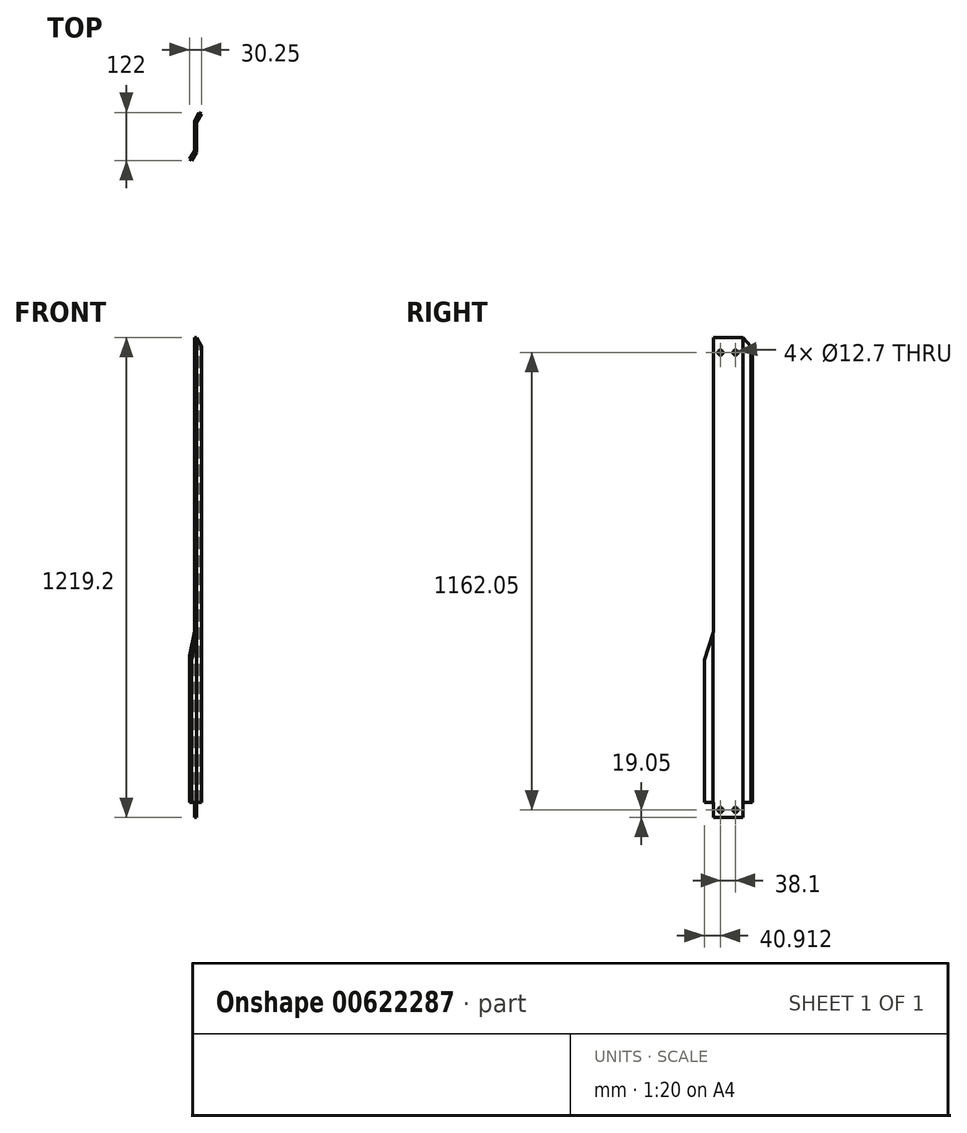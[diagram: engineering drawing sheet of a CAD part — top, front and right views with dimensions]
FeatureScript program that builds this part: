
annotation { "Feature Type Name" : "Feature", "Feature Type Description" : "" }
export const myFeature = defineFeature(function(context is Context, id is Id, definition is map)
    precondition{}
    {
        {
            var Q0;
            Q0=qCreatedBy(makeId("Top.planeOp"),FACE);
            var sketch = newSketch(context, id + "F0", { "sketchPlane" : qUnion([Q0])});
            skLineSegment(sketch, "E0.left", {"start": v(0, 0) * mm, "end": v(0, 76.2) * mm});
            skLineSegment(sketch, "E0.right", {"start": v(5.88, -1.67) * mm, "end": v(5.88, 74.53) * mm});
            skLineSegment(sketch, "E1", {"start": v(0, 76.2) * mm, "end": v(12.2, 98.47) * mm});
            skLineSegment(sketch, "E2", {"start": v(12.2, 98.47) * mm, "end": v(17.78, 95.42) * mm});
            skLineSegment(sketch, "E3", {"start": v(17.78, 95.42) * mm, "end": v(5.88, 74.53) * mm});
            skLineSegment(sketch, "E4", {"start": v(0, 0) * mm, "end": v(-12.47, -20.19) * mm});
            skLineSegment(sketch, "E5", {"start": v(-12.47, -20.19) * mm, "end": v(-7.06, -23.53) * mm});
            skLineSegment(sketch, "E6", {"start": v(-7.06, -23.53) * mm, "end": v(5.88, -1.67) * mm});
            skSolve(sketch);
        }
        {
            var Q0;
            Q0=makeQuery(id+"F0.imprint","IMPRINT",FACE,{"disambiguationData":[TD([[makeQuery(id+"F0.imprint","IMPRINT",EDGE,{"derivedFrom":sQuery(id+"F0.wireOp",EDGE,"E0.left")}),-1.0]])]});
            extrude(context, id + "F1", {"entities" : qUnion([Q0]), "oppositeDirection" : true, "depth" : 1219.2 * mm, "offsetDistance" : 25.4 * mm});
        }
        {
            var Q0;
            Q0=qCreatedBy(makeId("Right.planeOp"),FACE);
            var sketch = newSketch(context, id + "F2", { "sketchPlane" : qUnion([Q0])});
            skLineSegment(sketch, "E7.bottom", {"start": v(74.53, -1219.2) * mm, "end": v(98.47, -1219.2) * mm});
            skLineSegment(sketch, "E7.top", {"start": v(74.53, -1181.1) * mm, "end": v(98.47, -1181.1) * mm});
            skLineSegment(sketch, "E7.left", {"start": v(74.53, -1219.2) * mm, "end": v(74.53, -1181.1) * mm});
            skLineSegment(sketch, "E7.right", {"start": v(98.47, -1219.2) * mm, "end": v(98.47, -1181.1) * mm});
            skSolve(sketch);
        }
        {
            var Q0;
            Q0=makeQuery(id+"F2.imprint","IMPRINT",FACE,{"disambiguationData":[TD([[makeQuery(id+"F2.imprint","IMPRINT",EDGE,{"derivedFrom":sQuery(id+"F2.wireOp",EDGE,"E7.bottom")}),1.0]])]});
            extrude(context, id + "F3", {"entities" : qUnion([Q0]), "operationType" : NewBodyOperationType.REMOVE, "endBound" : BoundingType.THROUGH_ALL, "depth" : 25.4 * mm, "offsetDistance" : 25.4 * mm});
        }
        {
            var Q0;
            Q0=makeQuery(id+"F1.opExtrude","SWEPT_FACE",FACE,{"disambiguationData":[OSD([sQuery(id+"F0.wireOp",EDGE,"E0.right")])]});
            var sketch = newSketch(context, id + "F4", { "sketchPlane" : qUnion([Q0])});
            skPoint(sketch, "E8", {"position": v(17.38, -1200.15) * mm});
            skPoint(sketch, "E9", {"position": v(55.48, -1200.15) * mm});
            skPoint(sketch, "E10", {"position": v(98.49, -25.4) * mm});
            skPoint(sketch, "E11", {"position": v(-22.33, -25.4) * mm});
            skLineSegment(sketch, "E12", {"start": v(74.53, 0) * mm, "end": v(98.49, -25.4) * mm});
            skLineSegment(sketch, "E13", {"start": v(98.49, 0) * mm, "end": v(74.53, 0) * mm});
            skLineSegment(sketch, "E14", {"start": v(-22.33, -25.4) * mm, "end": v(-1.67, 0) * mm});
            skLineSegment(sketch, "E15", {"start": v(-1.67, 0) * mm, "end": v(-22.33, 0) * mm});
            skLineSegment(sketch, "E16", {"start": v(-22.33, 0) * mm, "end": v(-22.33, -25.4) * mm});
            skLineSegment(sketch, "E17", {"start": v(98.49, 0) * mm, "end": v(98.49, -25.4) * mm});
            skSolve(sketch);
        }
        {
            var Q0;
            Q0=sQuery(id+"F4.wireOp",VERTEX,"E9");
            var Q1;
            Q1=sQuery(id+"F4.wireOp",VERTEX,"E8");
            var Q2;
            Q2=makeQuery(id+"F1.opExtrude","SWEPT_BODY",BODY,{"disambiguationData":[OSD([sQuery(id+"F0.wireOp",EDGE,"E0.left"),sQuery(id+"F0.wireOp",EDGE,"E0.right"),sQuery(id+"F0.wireOp",EDGE,"E1"),sQuery(id+"F0.wireOp",EDGE,"E2"),sQuery(id+"F0.wireOp",EDGE,"E3"),sQuery(id+"F0.wireOp",EDGE,"E4"),sQuery(id+"F0.wireOp",EDGE,"E5"),sQuery(id+"F0.wireOp",EDGE,"E6")])]});
            hole(context, id + "F5", {"style" : HoleStyle.SIMPLE, "endStyle" : HoleEndStyle.THROUGH, "holeDiameter" : 12.7 * mm, "majorDiameter" : 6.35 * mm, "isTappedThrough" : true, "tappedDepth" : 12.7 * mm, "tapClearance" : 3, "startFromSketch" : true, "locations" : qUnion([Q0, Q1]), "scope" : qUnion([Q2])});
        }
        {
            var Q0;
            Q0=makeQuery(id+"F1.opExtrude","SWEPT_FACE",FACE,{"disambiguationData":[OSD([sQuery(id+"F0.wireOp",EDGE,"E0.right")])]});
            var sketch = newSketch(context, id + "F6", { "sketchPlane" : qUnion([Q0])});
            skPoint(sketch, "E18", {"position": v(55.48, -38.1) * mm});
            skPoint(sketch, "E19", {"position": v(17.38, -38.1) * mm});
            skSolve(sketch);
        }
        {
            var Q0;
            Q0=sQuery(id+"F6.wireOp",VERTEX,"E18");
            var Q1;
            Q1=sQuery(id+"F6.wireOp",VERTEX,"E19");
            var Q2;
            Q2=makeQuery(id+"F1.opExtrude","SWEPT_BODY",BODY,{"disambiguationData":[OSD([sQuery(id+"F0.wireOp",EDGE,"E0.left"),sQuery(id+"F0.wireOp",EDGE,"E0.right"),sQuery(id+"F0.wireOp",EDGE,"E1"),sQuery(id+"F0.wireOp",EDGE,"E2"),sQuery(id+"F0.wireOp",EDGE,"E3"),sQuery(id+"F0.wireOp",EDGE,"E4"),sQuery(id+"F0.wireOp",EDGE,"E5"),sQuery(id+"F0.wireOp",EDGE,"E6")])]});
            hole(context, id + "F7", {"style" : HoleStyle.SIMPLE, "endStyle" : HoleEndStyle.THROUGH, "holeDiameter" : 12.7 * mm, "majorDiameter" : 6.35 * mm, "isTappedThrough" : true, "tappedDepth" : 12.7 * mm, "tapClearance" : 3, "startFromSketch" : true, "locations" : qUnion([Q0, Q1]), "scope" : qUnion([Q2])});
        }
        {
            var Q0;
            Q0 = qSketchRegion(id + "F4", true);
            extrude(context, id + "F8", {"entities" : qUnion([Q0]), "operationType" : NewBodyOperationType.REMOVE, "endBound" : BoundingType.THROUGH_ALL, "oppositeDirection" : true, "depth" : 25.4 * mm, "offsetDistance" : 25.4 * mm});
        }
        {
            var Q0;
            Q0 = qSketchRegion(id + "F4", true);
            var Q1;
            Q1=makeQuery(id+"F1.opExtrude","SWEPT_FACE",FACE,{"disambiguationData":[OSD([sQuery(id+"F0.wireOp",EDGE,"E3")])]});
            extrude(context, id + "F9", {"entities" : qUnion([Q0, Q1]), "operationType" : NewBodyOperationType.REMOVE, "depth" : 25.4 * mm, "offsetDistance" : 25.4 * mm});
        }
        {
            var Q0;
            Q0=makeQuery(id+"F1.opExtrude","SWEPT_FACE",FACE,{"disambiguationData":[OSD([sQuery(id+"F0.wireOp",EDGE,"E0.right")])]});
            var sketch = newSketch(context, id + "F10", { "sketchPlane" : qUnion([Q0])});
            skLineSegment(sketch, "E20.bottom", {"start": v(0, -1219.2) * mm, "end": v(-23.53, -1219.2) * mm});
            skLineSegment(sketch, "E20.top", {"start": v(0, -1181.1) * mm, "end": v(-23.53, -1181.1) * mm});
            skLineSegment(sketch, "E20.left", {"start": v(0, -1219.2) * mm, "end": v(0, -1181.1) * mm});
            skLineSegment(sketch, "E20.right", {"start": v(-23.53, -1219.2) * mm, "end": v(-23.53, -1181.1) * mm});
            skSolve(sketch);
        }
        {
            var Q0;
            Q0 = qSketchRegion(id + "F10", true);
            extrude(context, id + "F11", {"entities" : qUnion([Q0]), "operationType" : NewBodyOperationType.REMOVE, "oppositeDirection" : true, "depth" : 25.4 * mm, "offsetDistance" : 25.4 * mm});
        }
        {
            var Q0;
            Q0=makeQuery(id+"F1.opExtrude","SWEPT_FACE",FACE,{"disambiguationData":[OSD([sQuery(id+"F0.wireOp",EDGE,"E0.right")])]});
            var sketch = newSketch(context, id + "F12", { "sketchPlane" : qUnion([Q0])});
            skLineSegment(sketch, "E21.bottom", {"start": v(0, 0) * mm, "end": v(-23.53, 0) * mm});
            skLineSegment(sketch, "E21.left", {"start": v(0, 0) * mm, "end": v(0, -746.36) * mm});
            skLineSegment(sketch, "E21.right", {"start": v(-23.53, 0) * mm, "end": v(-23.53, -746.36) * mm});
            skLineSegment(sketch, "E22", {"start": v(0, -746.36) * mm, "end": v(-23.53, -819.47) * mm});
            skLineSegment(sketch, "E23", {"start": v(-23.53, -819.47) * mm, "end": v(-23.53, -746.36) * mm});
            skSolve(sketch);
        }
        {
            var Q0;
            Q0 = qSketchRegion(id + "F12", true);
            extrude(context, id + "F13", {"entities" : qUnion([Q0]), "operationType" : NewBodyOperationType.REMOVE, "oppositeDirection" : true, "depth" : 25.4 * mm, "offsetDistance" : 25.4 * mm});
        }
    });
